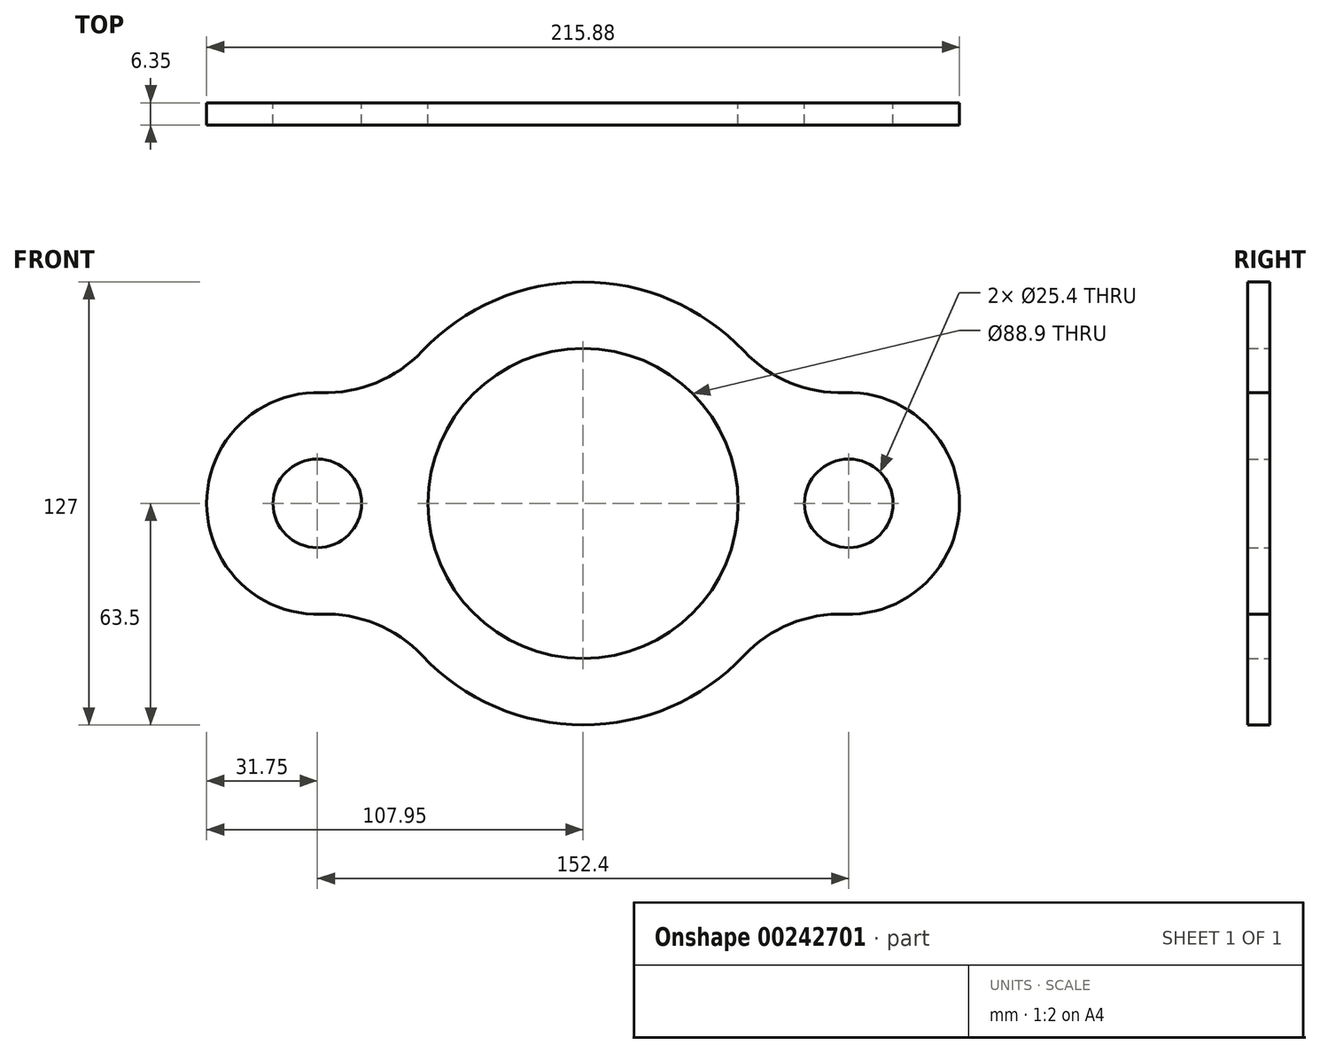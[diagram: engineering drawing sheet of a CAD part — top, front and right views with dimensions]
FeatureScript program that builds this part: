
annotation { "Feature Type Name" : "Feature", "Feature Type Description" : "" }
export const myFeature = defineFeature(function(context is Context, id is Id, definition is map)
    precondition{}
    {
        {
            var Q0;
            Q0=qCreatedBy(makeId("Front.planeOp"),FACE);
            var sketch = newSketch(context, id + "F0", { "sketchPlane" : qUnion([Q0])});
            skArc(sketch, "E0", {"start": v(-46.14, -43.63) * mm, "mid": v(0, -63.5) * mm, "end": v(46.14, -43.63) * mm});
            skCircle(sketch, "E1", {"center": v(0, 0) * mm, "radius": 44.45 * mm});
            skCircle(sketch, "E2", {"center": v(76.2, 0) * mm, "radius": 12.7 * mm});
            skCircle(sketch, "E3", {"center": v(-76.2, 0) * mm, "radius": 12.7 * mm});
            skArc(sketch, "E4", {"start": v(-75.12, 31.73) * mm, "mid": v(-107.95, 0) * mm, "end": v(-75.12, -31.73) * mm});
            skArc(sketch, "E5.trimOffspring", {"start": v(75.1, -31.73) * mm, "mid": v(107.93, 0) * mm, "end": v(75.1, 31.73) * mm});
            skArc(sketch, "E6.trimOffspring", {"start": v(46.14, 43.63) * mm, "mid": v(0, 63.5) * mm, "end": v(-46.14, 43.63) * mm});
            skArc(sketch, "E7.filletArc", {"start": v(-75.12, 31.73) * mm, "mid": v(-59.35, 34.56) * mm, "end": v(-46.14, 43.63) * mm});
            skArc(sketch, "E8.filletArc", {"start": v(46.14, 43.63) * mm, "mid": v(59.34, 34.57) * mm, "end": v(75.1, 31.73) * mm});
            skArc(sketch, "E9.filletArc", {"start": v(75.1, -31.73) * mm, "mid": v(59.34, -34.57) * mm, "end": v(46.14, -43.63) * mm});
            skArc(sketch, "E10.filletArc", {"start": v(-46.14, -43.63) * mm, "mid": v(-59.35, -34.56) * mm, "end": v(-75.12, -31.73) * mm});
            skSolve(sketch);
        }
        {
            var Q0;
            Q0 = qSketchRegion(id + "F0", true);
            extrude(context, id + "F1", {"entities" : qUnion([Q0]), "depth" : 6.35 * mm});
        }
    });
